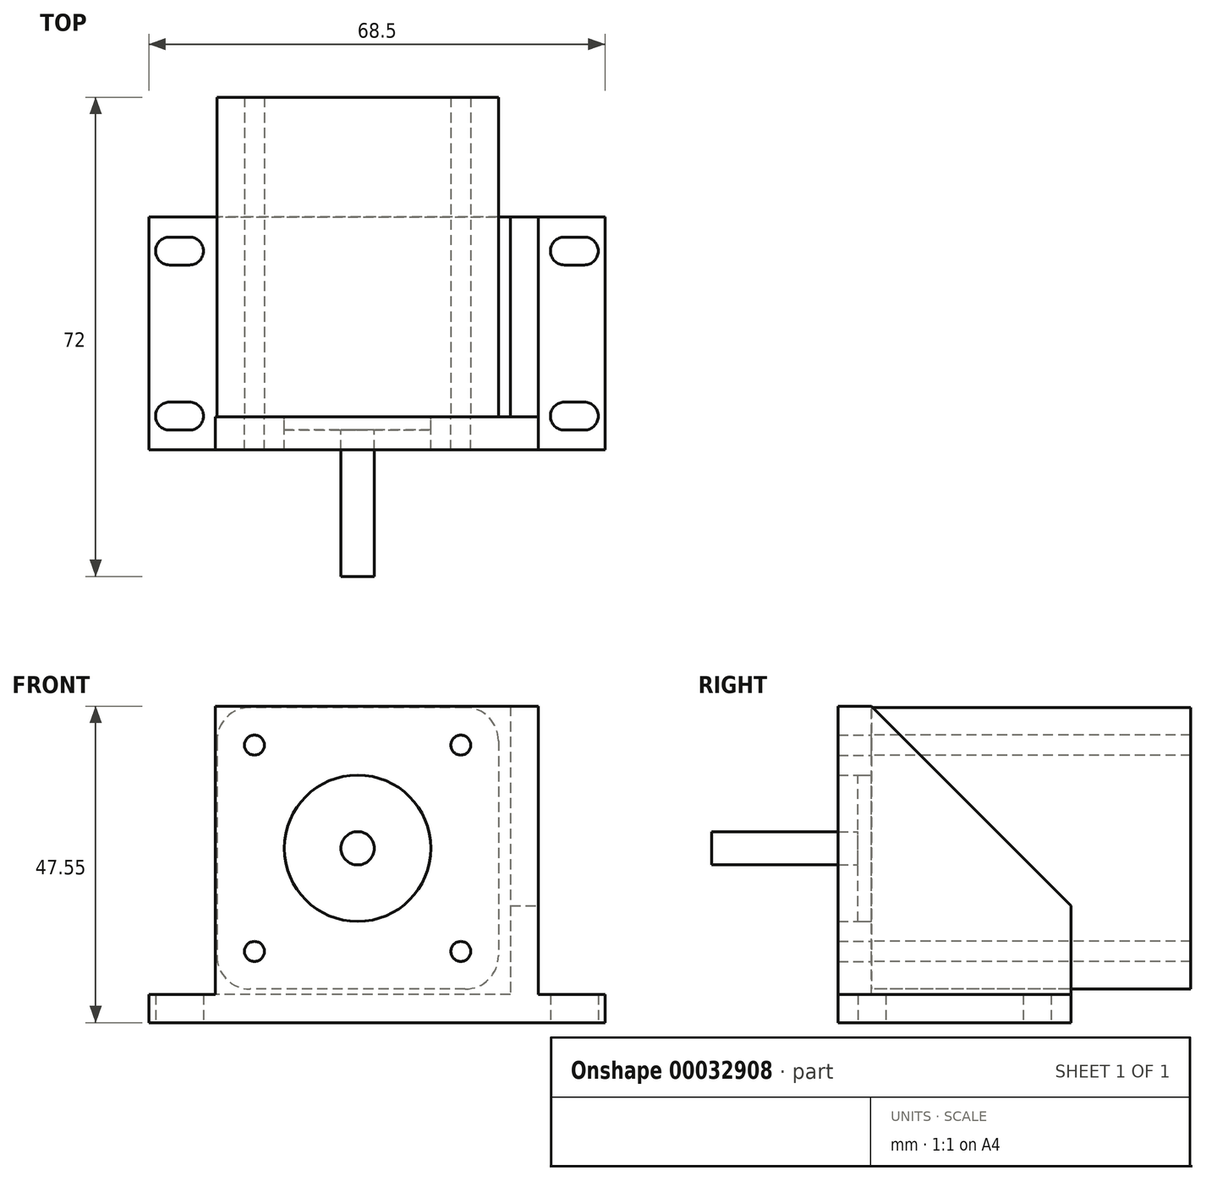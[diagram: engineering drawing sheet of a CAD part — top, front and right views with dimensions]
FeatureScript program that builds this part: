
annotation { "Feature Type Name" : "Feature", "Feature Type Description" : "" }
export const myFeature = defineFeature(function(context is Context, id is Id, definition is map)
    precondition{}
    {
        {
            var Q0;
            Q0=qCreatedBy(makeId("Front.planeOp"),FACE);
            var sketch = newSketch(context, id + "F0", { "sketchPlane" : qUnion([Q0])});
            skCircle(sketch, "E0", {"center": v(0, 0) * mm, "radius": 11 * mm});
            skCircle(sketch, "E1", {"center": v(0, 0) * mm, "radius": 2.5 * mm});
            skLineSegment(sketch, "E2.bottom", {"start": v(21.15, 21.15) * mm, "end": v(-21.15, 21.15) * mm});
            skLineSegment(sketch, "E2.top", {"start": v(21.15, -21.15) * mm, "end": v(-21.15, -21.15) * mm});
            skLineSegment(sketch, "E2.left", {"start": v(21.15, 21.15) * mm, "end": v(21.15, -21.15) * mm});
            skLineSegment(sketch, "E2.right", {"start": v(-21.15, 21.15) * mm, "end": v(-21.15, -21.15) * mm});
            skCircle(sketch, "E3", {"center": v(15.5, 15.5) * mm, "radius": 1.5 * mm});
            skLineSegment(sketch, "E4", {"start": v(0, 21.15) * mm, "end": v(0, -21.15) * mm, "construction": true});
            skLineSegment(sketch, "E5", {"start": v(21.15, 0) * mm, "end": v(-21.15, 0) * mm, "construction": true});
            skCircle(sketch, "E6.MirrorC", {"center": v(-15.5, 15.5) * mm, "radius": 1.5 * mm});
            skCircle(sketch, "E7.MirrorC", {"center": v(-15.5, -15.5) * mm, "radius": 1.5 * mm});
            skCircle(sketch, "E8.MirrorC", {"center": v(15.5, -15.5) * mm, "radius": 1.5 * mm});
            skSolve(sketch);
        }
        {
            var Q0;
            Q0=makeQuery(id+"F0.imprint","IMPRINT",FACE,{"disambiguationData":[TD([[makeQuery(id+"F0.imprint","IMPRINT",EDGE,{"derivedFrom":sQuery(id+"F0.wireOp",EDGE,"E1")}),1.0]])]});
            extrude(context, id + "F1", {"entities" : qUnion([Q0]), "depth" : 24 * mm});
        }
        {
            var Q0;
            Q0=makeQuery(id+"F0.imprint","IMPRINT",FACE,{"disambiguationData":[TD([[makeQuery(id+"F0.imprint","IMPRINT",EDGE,{"derivedFrom":sQuery(id+"F0.wireOp",EDGE,"E0")}),1.0]])]});
            extrude(context, id + "F2", {"entities" : qUnion([Q0]), "operationType" : NewBodyOperationType.ADD, "depth" : 2 * mm});
        }
        {
            var Q0;
            Q0=makeQuery(id+"F0.imprint","IMPRINT",FACE,{"disambiguationData":[TD([[makeQuery(id+"F0.imprint","IMPRINT",EDGE,{"derivedFrom":sQuery(id+"F0.wireOp",EDGE,"E1")}),1.0]])]});
            var Q1;
            Q1=makeQuery(id+"F0.imprint","IMPRINT",FACE,{"disambiguationData":[TD([[makeQuery(id+"F0.imprint","IMPRINT",EDGE,{"derivedFrom":sQuery(id+"F0.wireOp",EDGE,"E0")}),1.0]])]});
            var Q2;
            Q2=makeQuery(id+"F0.imprint","IMPRINT",FACE,{"disambiguationData":[TD([[makeQuery(id+"F0.imprint","IMPRINT",EDGE,{"derivedFrom":sQuery(id+"F0.wireOp",EDGE,"E0")}),-1.0]])]});
            extrude(context, id + "F3", {"entities" : qUnion([Q0, Q1, Q2]), "operationType" : NewBodyOperationType.ADD, "oppositeDirection" : true, "depth" : 48 * mm});
        }
        {
            var Q0;
            Q0=makeQuery(id+"F3.opExtrude","SWEPT_EDGE",EDGE,{"disambiguationData":[OSD([sQuery(id+"F0.wireOp",EDGE,"E2.bottom"),sQuery(id+"F0.wireOp",EDGE,"E2.left")])]});
            var Q1;
            Q1=makeQuery(id+"F3.opExtrude","SWEPT_EDGE",EDGE,{"disambiguationData":[OSD([sQuery(id+"F0.wireOp",EDGE,"E2.top"),sQuery(id+"F0.wireOp",EDGE,"E2.left")])]});
            var Q2;
            Q2=makeQuery(id+"F3.opExtrude","SWEPT_EDGE",EDGE,{"disambiguationData":[OSD([sQuery(id+"F0.wireOp",EDGE,"E2.top"),sQuery(id+"F0.wireOp",EDGE,"E2.right")])]});
            var Q3;
            Q3=makeQuery(id+"F3.opExtrude","SWEPT_EDGE",EDGE,{"disambiguationData":[OSD([sQuery(id+"F0.wireOp",EDGE,"E2.bottom"),sQuery(id+"F0.wireOp",EDGE,"E2.right")])]});
            fillet(context, id + "F4", {"entities" : qUnion([Q0, Q1, Q2, Q3]), "radius" : 5 * mm, "tangentPropagation" : true, "allowEdgeOverflow" : false});
        }
        {
            var Q0;
            Q0=makeQuery(id+"F3.opExtrude","CAP_FACE",FACE,{"disambiguationData":[OSD([sQuery(id+"F0.wireOp",EDGE,"E2.bottom"),sQuery(id+"F0.wireOp",EDGE,"E2.top"),sQuery(id+"F0.wireOp",EDGE,"E2.left"),sQuery(id+"F0.wireOp",EDGE,"E2.right"),sQuery(id+"F0.wireOp",EDGE,"E3"),sQuery(id+"F0.wireOp",EDGE,"E6.MirrorC"),sQuery(id+"F0.wireOp",EDGE,"E7.MirrorC"),sQuery(id+"F0.wireOp",EDGE,"E8.MirrorC")])],"isStart":true});
            var sketch = newSketch(context, id + "F5", { "sketchPlane" : qUnion([Q0])});
            skLineSegment(sketch, "E9", {"start": v(-21.35, -22) * mm, "end": v(-21.35, 21.35) * mm});
            skLineSegment(sketch, "E10", {"start": v(-21.35, 21.35) * mm, "end": v(27.15, 21.35) * mm});
            skLineSegment(sketch, "E11", {"start": v(27.15, 21.35) * mm, "end": v(27.15, -22) * mm});
            skLineSegment(sketch, "E12", {"start": v(27.15, -22) * mm, "end": v(-21.35, -22) * mm});
            skLineSegment(sketch, "E13", {"start": v(-21.35, -26.2) * mm, "end": v(27.15, -26.2) * mm});
            skCircle(sketch, "E14.0", {"center": v(15.5, 15.5) * mm, "radius": 1.5 * mm});
            skCircle(sketch, "E14.1", {"center": v(-15.5, 15.5) * mm, "radius": 1.5 * mm});
            skCircle(sketch, "E14.2", {"center": v(-15.5, -15.5) * mm, "radius": 1.5 * mm});
            skCircle(sketch, "E14.3", {"center": v(15.5, -15.5) * mm, "radius": 1.5 * mm});
            skCircle(sketch, "E15", {"center": v(0, 0) * mm, "radius": 6.25 * mm, "construction": true});
            skCircle(sketch, "E16", {"center": v(-25, 0) * mm, "radius": 18.75 * mm, "construction": true});
            skCircle(sketch, "E17", {"center": v(-25, 0) * mm, "radius": 5 * mm, "construction": true});
            skCircle(sketch, "E18.0", {"center": v(0, 0) * mm, "radius": 11 * mm});
            skCircle(sketch, "E19", {"center": v(-25, 0) * mm, "radius": 20 * mm, "construction": true});
            skLineSegment(sketch, "E20", {"start": v(-21.35, -22) * mm, "end": v(-21.35, -26.2) * mm});
            skLineSegment(sketch, "E21", {"start": v(27.15, -22) * mm, "end": v(27.15, -26.2) * mm});
            skLineSegment(sketch, "E22", {"start": v(22.95, 21.35) * mm, "end": v(22.95, -22) * mm});
            skLineSegment(sketch, "E23", {"start": v(-21.35, -22) * mm, "end": v(-31.35, -22) * mm});
            skLineSegment(sketch, "E24", {"start": v(-31.35, -22) * mm, "end": v(-31.35, -26.2) * mm});
            skLineSegment(sketch, "E25", {"start": v(-31.35, -26.2) * mm, "end": v(-21.35, -26.2) * mm});
            skLineSegment(sketch, "E26", {"start": v(27.15, -26.2) * mm, "end": v(37.15, -26.2) * mm});
            skLineSegment(sketch, "E27", {"start": v(37.15, -26.2) * mm, "end": v(37.15, -22) * mm});
            skLineSegment(sketch, "E28", {"start": v(37.15, -22) * mm, "end": v(27.15, -22) * mm});
            skSolve(sketch);
        }
        {
            var Q0;
            {var subQ0=sQuery(id+"F5.wireOp",EDGE,"E11");Q0=makeQuery(id+"F5.imprint","IMPRINT",FACE,{"disambiguationData":[TD([[makeQuery(id+"F5.imprint","IMPRINT",EDGE,{"derivedFrom":subQ0}),-1.0]])]});}
            var Q1;
            Q1=makeQuery(id+"F5.imprint","IMPRINT",FACE,{"disambiguationData":[TD([[makeQuery(id+"F5.imprint","IMPRINT",EDGE,{"derivedFrom":sQuery(id+"F5.wireOp",EDGE,"E13")}),1.0]])]});
            var Q2;
            Q2=makeQuery(id+"F5.imprint","IMPRINT",FACE,{"disambiguationData":[TD([[makeQuery(id+"F5.imprint","IMPRINT",EDGE,{"derivedFrom":sQuery(id+"F5.wireOp",EDGE,"E21")}),1.0]])]});
            var Q3;
            Q3=makeQuery(id+"F5.imprint","IMPRINT",FACE,{"disambiguationData":[TD([[makeQuery(id+"F5.imprint","IMPRINT",EDGE,{"derivedFrom":sQuery(id+"F5.wireOp",EDGE,"E20")}),-1.0]])]});
            var Q4;
            {var subQ6=sQuery(id+"F5.wireOp",EDGE,"E9");Q4=makeQuery(id+"F5.imprint","IMPRINT",FACE,{"disambiguationData":[TD([[makeQuery(id+"F5.imprint","IMPRINT",EDGE,{"derivedFrom":subQ6}),-1.0]])]});}
            var Q5;
            Q5=makeQuery(id+"F5.imprint","IMPRINT",FACE,{"disambiguationData":[TD([[makeQuery(id+"F5.imprint","IMPRINT",EDGE,{"derivedFrom":sQuery(id+"F5.wireOp",EDGE,"E14.0")}),-1.0]])]});
            extrude(context, id + "F6", {"entities" : qUnion([Q0, Q1, Q2, Q3, Q4, Q5]), "depth" : 5 * mm});
        }
        {
            var Q0;
            Q0=makeQuery(id+"F5.imprint","IMPRINT",FACE,{"disambiguationData":[TD([[makeQuery(id+"F5.imprint","IMPRINT",EDGE,{"derivedFrom":sQuery(id+"F5.wireOp",EDGE,"E13")}),1.0]])]});
            var Q1;
            Q1=makeQuery(id+"F5.imprint","IMPRINT",FACE,{"disambiguationData":[TD([[makeQuery(id+"F5.imprint","IMPRINT",EDGE,{"derivedFrom":sQuery(id+"F5.wireOp",EDGE,"E21")}),1.0]])]});
            var Q2;
            {var subQ0=sQuery(id+"F5.wireOp",EDGE,"E11");Q2=makeQuery(id+"F5.imprint","IMPRINT",FACE,{"disambiguationData":[TD([[makeQuery(id+"F5.imprint","IMPRINT",EDGE,{"derivedFrom":subQ0}),-1.0]])]});}
            var Q3;
            Q3=makeQuery(id+"F5.imprint","IMPRINT",FACE,{"disambiguationData":[TD([[makeQuery(id+"F5.imprint","IMPRINT",EDGE,{"derivedFrom":sQuery(id+"F5.wireOp",EDGE,"E20")}),-1.0]])]});
            extrude(context, id + "F7", {"entities" : qUnion([Q0, Q1, Q2, Q3]), "operationType" : NewBodyOperationType.ADD, "oppositeDirection" : true, "depth" : 30 * mm});
        }
        {
            var Q0;
            Q0=makeQuery(id+"F7.opExtrude","CAP_EDGE",EDGE,{"disambiguationData":[OSD([sQuery(id+"F5.wireOp",EDGE,"E10")])],"isStart":false});
            chamfer(context, id + "F8", {"entities" : qUnion([Q0]), "width" : 30 * mm, "tangentPropagation" : true});
        }
        {
            var Q0;
            {var subQ0=sQuery(id+"F5.wireOp",EDGE,"E26");var subQ1=sQuery(id+"F5.wireOp",EDGE,"E25");var subQ2=sQuery(id+"F5.wireOp",EDGE,"E13");Q0=makeQuery(id+"F7.boolean.opBoolean","MERGE",FACE,{"derivedFrom":[makeQuery(id+"F6.opExtrude","SWEPT_FACE",FACE,{"disambiguationData":[OSD([subQ2,subQ1,subQ0])]}),makeQuery(id+"F7.opExtrude","SWEPT_FACE",FACE,{"disambiguationData":[OSD([subQ2,subQ1,subQ0])]})]});}
            var sketch = newSketch(context, id + "F9", { "sketchPlane" : qUnion([Q0])});
            skLineSegment(sketch, "E29", {"start": v(2.9, -30) * mm, "end": v(2.9, 5) * mm, "construction": true});
            skLineSegment(sketch, "E30", {"start": v(-31.35, -12.5) * mm, "end": v(37.15, -12.5) * mm, "construction": true});
            skArc(sketch, "E31", {"start": v(31.05, -27) * mm, "mid": v(28.95, -24.9) * mm, "end": v(31.05, -22.8) * mm});
            skArc(sketch, "E32", {"start": v(34.05, -22.8) * mm, "mid": v(36.15, -24.9) * mm, "end": v(34.05, -27) * mm});
            skLineSegment(sketch, "E33", {"start": v(31.05, -22.8) * mm, "end": v(34.05, -22.8) * mm});
            skLineSegment(sketch, "E34", {"start": v(31.05, -27) * mm, "end": v(34.05, -27) * mm});
            skLineSegment(sketch, "E35", {"start": v(31.05, -24.9) * mm, "end": v(34.05, -24.9) * mm, "construction": true});
            skPoint(sketch, "E36", {"position": v(32.55, -24.9) * mm});
            skArc(sketch, "E37.MirrorCS", {"start": v(34.05, -27) * mm, "mid": v(36.15, -24.9) * mm, "end": v(34.05, -22.8) * mm});
            skArc(sketch, "E38.MirrorCS", {"start": v(31.05, -22.8) * mm, "mid": v(28.95, -24.9) * mm, "end": v(31.05, -27) * mm});
            skLineSegment(sketch, "E39.MirrorCS", {"start": v(31.05, -0.1) * mm, "end": v(34.05, -0.1) * mm, "construction": true});
            skArc(sketch, "E40.MirrorCS", {"start": v(31.05, 2) * mm, "mid": v(28.95, -0.1) * mm, "end": v(31.05, -2.2) * mm});
            skArc(sketch, "E41.MirrorCS", {"start": v(34.05, -2.2) * mm, "mid": v(36.15, -0.1) * mm, "end": v(34.05, 2) * mm});
            skPoint(sketch, "E42.MirrorP", {"position": v(32.55, -0.1) * mm});
            skLineSegment(sketch, "E43.MirrorCS", {"start": v(31.05, -2.2) * mm, "end": v(34.05, -2.2) * mm});
            skLineSegment(sketch, "E44.MirrorCS", {"start": v(31.05, 2) * mm, "end": v(34.05, 2) * mm});
            skArc(sketch, "E45.MirrorCS", {"start": v(31.05, -2.2) * mm, "mid": v(28.95, -0.1) * mm, "end": v(31.05, 2) * mm});
            skArc(sketch, "E46.MirrorCS", {"start": v(34.05, 2) * mm, "mid": v(36.15, -0.1) * mm, "end": v(34.05, -2.2) * mm});
            skLineSegment(sketch, "E47.MirrorCS", {"start": v(-25.25, -0.1) * mm, "end": v(-28.25, -0.1) * mm, "construction": true});
            skLineSegment(sketch, "E48.MirrorCS", {"start": v(-25.25, -24.9) * mm, "end": v(-28.25, -24.9) * mm, "construction": true});
            skLineSegment(sketch, "E49.MirrorCS", {"start": v(-25.25, -27) * mm, "end": v(-28.25, -27) * mm});
            skArc(sketch, "E50.MirrorCS", {"start": v(-28.25, -2.2) * mm, "mid": v(-30.35, -0.1) * mm, "end": v(-28.25, 2) * mm});
            skArc(sketch, "E51.MirrorCS", {"start": v(-25.25, -2.2) * mm, "mid": v(-23.15, -0.1) * mm, "end": v(-25.25, 2) * mm});
            skArc(sketch, "E52.MirrorCS", {"start": v(-25.25, -27) * mm, "mid": v(-23.15, -24.9) * mm, "end": v(-25.25, -22.8) * mm});
            skLineSegment(sketch, "E53.MirrorCS", {"start": v(-25.25, -2.2) * mm, "end": v(-28.25, -2.2) * mm});
            skPoint(sketch, "E54.MirrorP", {"position": v(-26.75, -24.9) * mm});
            skLineSegment(sketch, "E55.MirrorCS", {"start": v(-25.25, -22.8) * mm, "end": v(-28.25, -22.8) * mm});
            skArc(sketch, "E56.MirrorCS", {"start": v(-28.25, -22.8) * mm, "mid": v(-30.35, -24.9) * mm, "end": v(-28.25, -27) * mm});
            skLineSegment(sketch, "E57.MirrorCS", {"start": v(-25.25, 2) * mm, "end": v(-28.25, 2) * mm});
            skPoint(sketch, "E58.MirrorP", {"position": v(-26.75, -0.1) * mm});
            skArc(sketch, "E59.MirrorCS", {"start": v(-28.25, 2) * mm, "mid": v(-30.35, -0.1) * mm, "end": v(-28.25, -2.2) * mm});
            skArc(sketch, "E60.MirrorCS", {"start": v(-25.25, -22.8) * mm, "mid": v(-23.15, -24.9) * mm, "end": v(-25.25, -27) * mm});
            skArc(sketch, "E61.MirrorCS", {"start": v(-25.25, 2) * mm, "mid": v(-23.15, -0.1) * mm, "end": v(-25.25, -2.2) * mm});
            skArc(sketch, "E62.MirrorCS", {"start": v(-28.25, -27) * mm, "mid": v(-30.35, -24.9) * mm, "end": v(-28.25, -22.8) * mm});
            skSolve(sketch);
        }
        {
            var Q0;
            Q0 = qSketchRegion(id + "F9", true);
            extrude(context, id + "F10", {"entities" : qUnion([Q0]), "operationType" : NewBodyOperationType.REMOVE, "endBound" : BoundingType.THROUGH_ALL, "oppositeDirection" : true, "depth" : 25 * mm});
        }
    });
